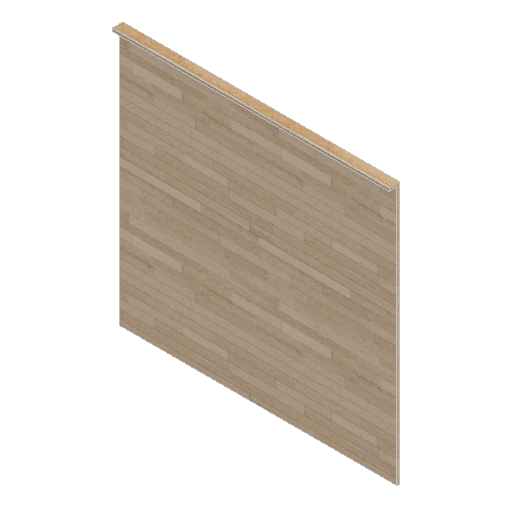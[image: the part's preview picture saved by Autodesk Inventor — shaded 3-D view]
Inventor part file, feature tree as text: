
AUTODESK INVENTOR PART (.ipt)
format: ipt  version: 2025.1 (Build 291241000, 241)  size: 272,384 bytes
history: native  units: mm
features: extrude x2, other x1
ambient origin geometry x8: Origin, YZ Plane, XZ Plane, XY Plane, X Axis, Y Axis, Z Axis, Center Point
bodies: Body1 (feature_tree)
feature tree (3):
  other  "Bryła1"
  extrude  "Wyciągnięcie proste1"  Depth=1800.0mm
  extrude  "Wyciągnięcie proste2"  Depth=1700.0mm
